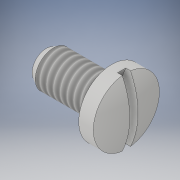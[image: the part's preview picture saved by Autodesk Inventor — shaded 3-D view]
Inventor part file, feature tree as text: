
AUTODESK INVENTOR PART (.ipt)
format: ipt  version: 2018.3 (Build 223284000, 284)  size: 148,480 bytes
history: native  units: in
note: dims shown in document units (in); Inventor stores cm internally (conversion verified against a paired STEP export)
features: sketch x2, revolve x1, thread x1, extrude x1
ambient origin geometry x8: Origin, YZ Plane, XZ Plane, XY Plane, X Axis, Y Axis, Z Axis, Center Point
bodies: Solid1 (feature_tree)
feature tree (5):
  revolve  "Revolution1"  [1 undecoded]
  thread  "Thread1"  [1 undecoded]
  extrude  "Extrusion1"  Depth=0.034in
  sketch  "Sketch1"  dims[d0=0.62in d1=0.1375in d2=0.06in]
  sketch  "Sketch2"  dims[d3=0.3614in d4=0.0314in d5=0.075in d6=0.01in d7=0.03in d8=30.0deg d9=90.0deg d10=0.595in d11=0.0in d12=0.636in d15=0.0414in d16=0.0914in d17=0.034in d18=0.0in]
note: 2 required parameter values undecoded (feature->parameter linkage not recoverable at this tier; creation-order binding heuristic only, values carry confidence <= 0.55)